# Revit family: ASH_Contour21_S6474_BIM_IT
name_source: partatom
category: Plumbing Fixtures
revit_build: Autodesk Revit 2017 (Build: 20160225_1515(x64)
units: mm (PartAtom-declared; Revit-internal decimal feet)

## family parameters
Always vertical = No
Cut with Voids When Loaded = No
OmniClass Number = 23.45.05.14.21.11
OmniClass Title = Bath/Shower Units
Part Type = Normal
Room Calculation Point = No
Round Connector Dimension = Use Diameter
Shared = No
Work Plane-Based = No

## types (1)
- S6474AC - MAIA MANIGLIONE 90X40CM BEU ANG.SX
    Accessori = www.idealstandard.it
    AltezzaNominale = 484 mm
    Autore = Ideal Standard
    BIMobject category = Accessories
    BIMobject category code = sanitary-accessories1
    BIMobject main category = Sanitary
    BIMobject main category code = sanitary
    BOSUseNativeGeometries = 1
    Brand = Ideal Standard
    Brand url = http://www.idealstandard.it
    Caratteristiche = Contour 21 - Maia Maniglione 900x400 mm Beu Ang.SX
    CodiceABarre = 5017830385080
    CodiceDiPrestazione = EN
    Connessione = piombatura
    CostoDiSostituzione = 0 $
    Date of publishing = 2019_01_04
    Description = Contour 21 - Maia Maniglione 900x400 mm Beu Ang.SX
    DescrizioneClassifcazioneUni2015 = Support rails
    Desrizione = Contour 21 - Maia Maniglione 900x400 mm Beu Ang.SX
    Dimensione = 400 x 500 x 35mm
    DimensioneScarico = 0
    EAN code = https://5017830385080
    Edition number = 1
    Finitura = Bianca
    Forma = Cilindro
    Garanzia = Garanzia Ideal Standard
    Grado = n/s
    IFC Classification = IfcSanitaryTerminal
    IfcEsportaCome = SanitaryTerminal
    InformazioniDiProdotto = http://www.idealstandard.it
    Installation instructions = http://www.idealstandard.it
    Installazione = http://www.idealstandard.it
    InstruzioniInstallazione = http://www.idealstandard.it
    LarghezzaNominale = 984 mm
    LunghezzaNominale = 118 mm
    Maniglia = No
    Manufacturer name = Ideal Standard
    Material main = Aluminium
    Materiale = Aluminium
    Model = S6474AC
    ModelloDiRiferimento = Contour 21 - Maia Maniglione 900x400 mm Beu Ang.SX
    NBS Reference Code = 45-35-72/360
    NBS Reference Description = Support Rails
    Nome = ISI_Upport Rails_Contour21_S6474AC_IdealStandard
    NomeOggettoBim = ISI_IdealStandard_Upport Rails_Contour21_S6474AC
    Nominal depth = 0
    Nominal height = 0
    NominalHeight = 484 mm
    NominalLength = 118 mm
    NominalWidth = 984 mm
    NumeroDiModello = S6474AC
    OmniClass Code = 23-31 25 00
    OmniClass Description = Toilet and Bath Specialties
    PartiDiRicambio = http://www.idealstandard.it
    PiattoDoccia = No
    Product Guid = 5765b2eb-6a60-41aa-88f7-c25e89580bdf
    Product SKU = S6474
    Product certification = http://www.idealstandard.it
    Product data url = https://bimobject.com
    Product family = CONTOUR21
    Product group = Accessories
    Product name = CONTOUR 21 GRBRAIL 90X40 BLUE ANGLD LH
    Product url = http://www.idealstandard.it
    ProfonditaNominale = 0 mm  [stored 0 ft]
    QR code = http://bimobject.com
    Revisione = 1
    RiferimentoClassificazioneUni2015 = Pr_40_20-76_84
    SeatMaterial = 0 mm  [stored 0 ft]
    SpessoreDelMateriale = 0
    SpilloverLivello = 0
    Technical description = http://www.idealstandard.it
    Telefono = 800 652 290
    TipoDiDato = Fisso
    TipoEspotazioneIfc = IfcSanitaryTerminalType
    URL = http://www.idealstandard.it
    Uniclass 1.4 Code = L2132
    Uniclass 1.4 Description = Rails
    Uniclass 2.0 Code = PR-85-85
    Uniclass 2.0 Description = Support Rails
    Uniclass 2015 Code = Pr_40_20-76_84
    Uniclass 2015 Name = Support rails
    UnitàDurata = anni
    UnitàDurataGaranzia = anni
    UnitàLineare = millimetri
    UnitàMonetaria = €
    UnitàSuperficie = €
    UnitàVolume = millimetri
    Versione = 1
    VersioneClassificazioneUni2015 = 1
    Weight Net (Kg) = 0
    Youtube clip = https://www.youtube.com

note: [stored X ft] marks values corroborated as IEEE doubles in the binary element streams (Revit-internal decimal feet)

## geometry (parser evidence)
native form markers: Sweep x1
no freeform markers — native parametric forms only
